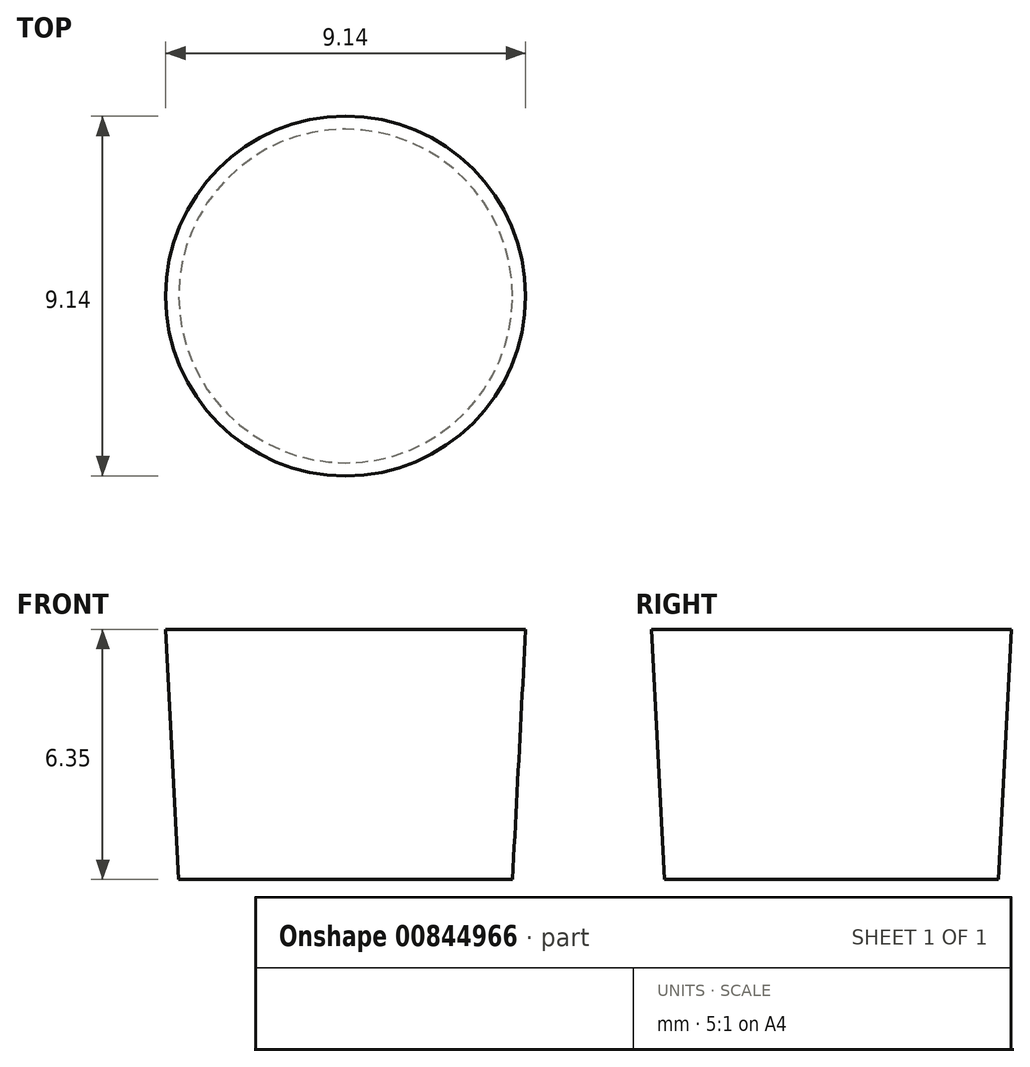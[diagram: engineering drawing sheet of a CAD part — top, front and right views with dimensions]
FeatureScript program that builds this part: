
annotation { "Feature Type Name" : "Feature", "Feature Type Description" : "" }
export const myFeature = defineFeature(function(context is Context, id is Id, definition is map)
    precondition{}
    {
        {
            var Q0;
            Q0=qCreatedBy(makeId("Top.planeOp"),FACE);
            var sketch = newSketch(context, id + "F0", { "sketchPlane" : qUnion([Q0])});
            skCircle(sketch, "E0", {"center": v(0, 0) * mm, "radius": 4.57 * mm});
            skSolve(sketch);
        }
        {
            var Q0;
            Q0=qSketchRegion(id+"F0",true);
            extrude(context, id + "F1", {"entities" : qUnion([Q0]), "oppositeDirection" : true, "depth" : 6.35 * mm, "offsetDistance" : 25.4 * mm, "hasDraft" : true, "draftAngle" : 3 * degree, "draftPullDirection" : true});
        }
    });
